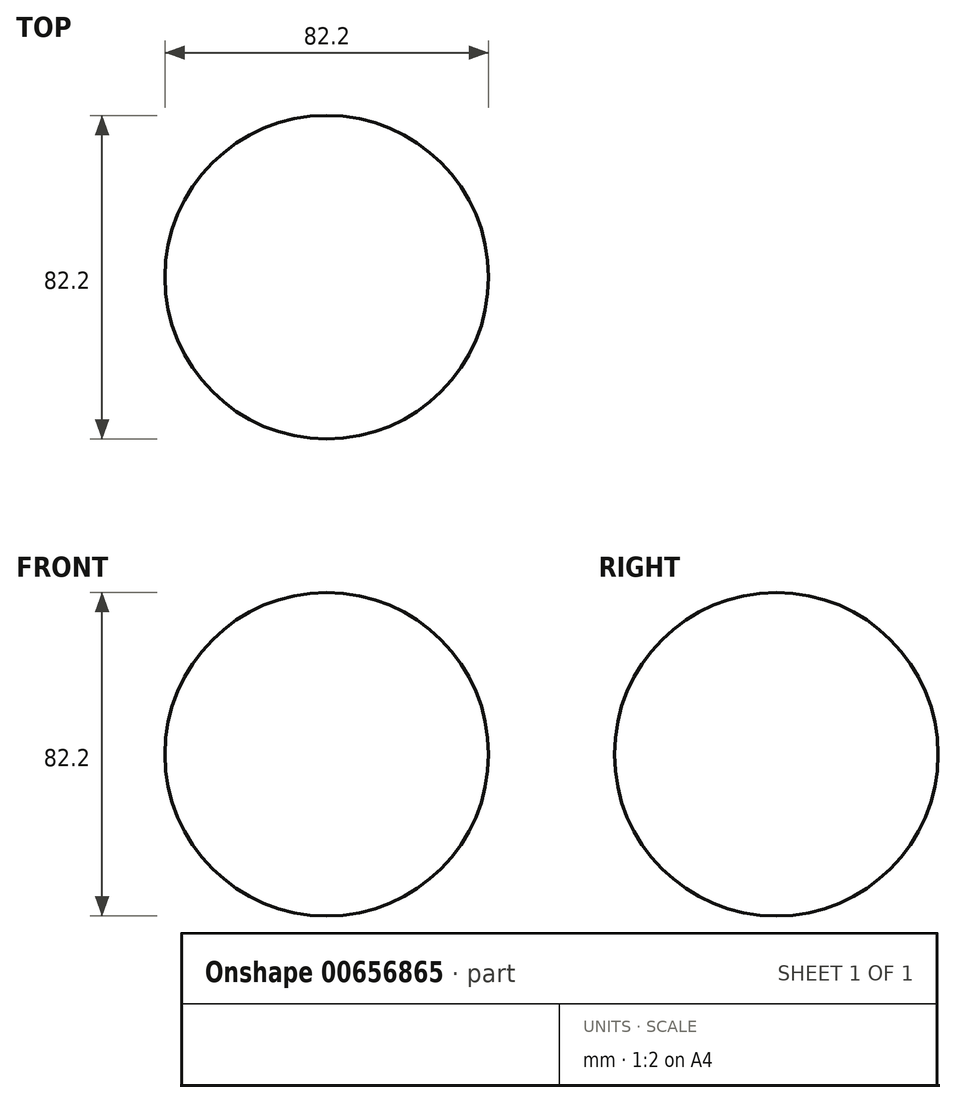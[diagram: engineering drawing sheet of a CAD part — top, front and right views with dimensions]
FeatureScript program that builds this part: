
annotation { "Feature Type Name" : "Feature", "Feature Type Description" : "" }
export const myFeature = defineFeature(function(context is Context, id is Id, definition is map)
    precondition{}
    {
        {
            var Q0;
            Q0=qCreatedBy(makeId("Top.planeOp"),FACE);
            var sketch = newSketch(context, id + "F0", { "sketchPlane" : qUnion([Q0])});
            skCircle(sketch, "E0", {"center": v(0, 0) * mm, "radius": 41.1 * mm});
            skLineSegment(sketch, "E1", {"start": v(0, -76.15) * mm, "end": v(0, 76.82) * mm});
            skSolve(sketch);
        }
        {
            var Q0;
            {var subQ0=sQuery(id+"F0.wireOp",EDGE,"E1");var subQ1=sQuery(id+"F0.wireOp",EDGE,"E0");var subQ2=makeQuery(id+"F0.imprint","INTERSECT",VERTEX,{"disambiguationData":[OD(0.0)],"derivedFrom":[subQ1,subQ0]});Q0=makeQuery(id+"F0.imprint","IMPRINT",FACE,{"disambiguationData":[TD([[makeQuery(id+"F0.imprint","IMPRINT",EDGE,{"disambiguationData":[TD([[subQ2,-1.0]])],"derivedFrom":subQ1}),1.0]])]});}
            var Q1;
            Q1=sQuery(id+"F0.wireOp",EDGE,"E1");
            revolve(context, id + "F1", {"entities" : qUnion([Q0]), "axis" : qUnion([Q1]), "revolveType" : RevolveType.FULL});
        }
    });
